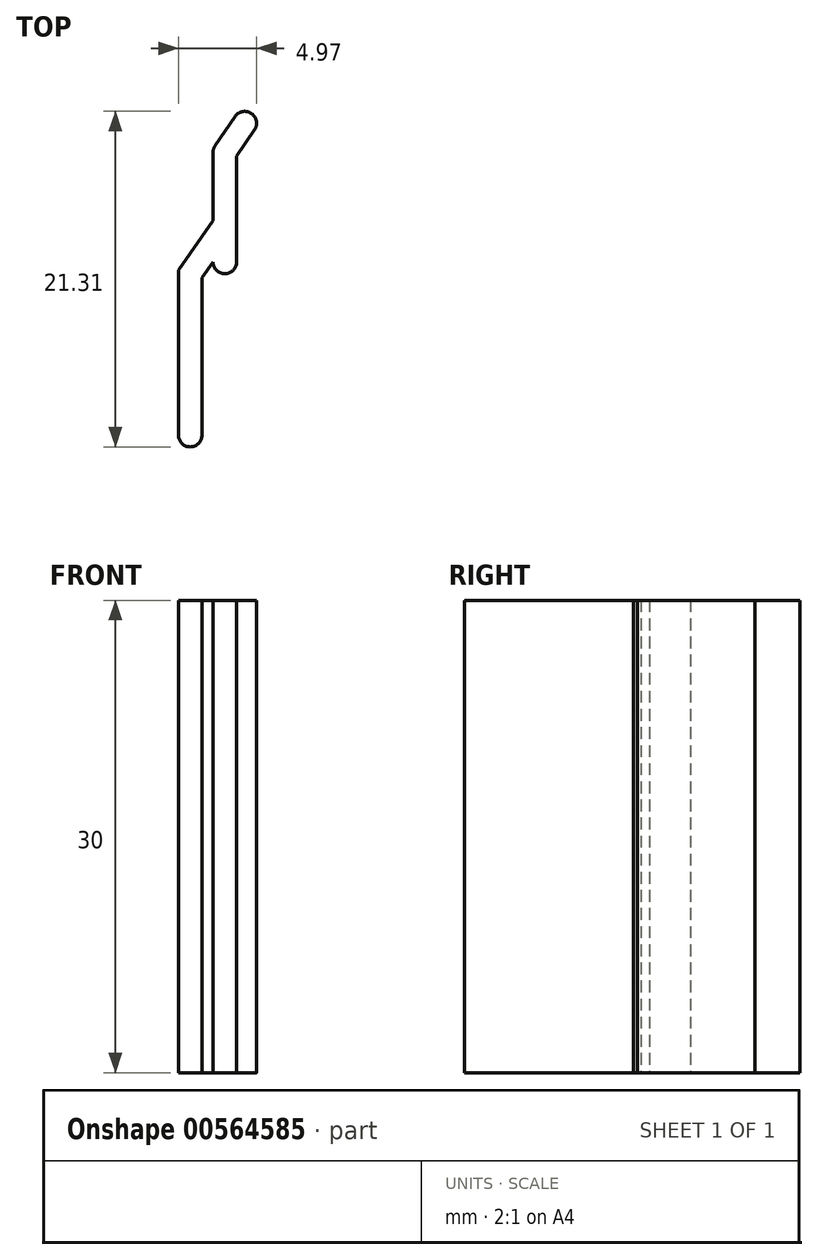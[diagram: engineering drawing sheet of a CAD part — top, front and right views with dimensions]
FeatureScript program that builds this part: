
annotation { "Feature Type Name" : "Feature", "Feature Type Description" : "" }
export const myFeature = defineFeature(function(context is Context, id is Id, definition is map)
    precondition{}
    {
        {
            var Q0;
            Q0=qCreatedBy(makeId("Top.planeOp"),FACE);
            var sketch = newSketch(context, id + "F0", { "sketchPlane" : qUnion([Q0])});
            skLineSegment(sketch, "E0", {"start": v(0, 0) * mm, "end": v(0, -6.95) * mm, "construction": true});
            skLineSegment(sketch, "E1", {"start": v(0, 0) * mm, "end": v(1.27, 1.86) * mm, "construction": true});
            skArc(sketch, "E2.0.startCap", {"start": v(-0.75, 0) * mm, "mid": v(-0.72, 0.22) * mm, "end": v(-0.62, 0.42) * mm});
            skArc(sketch, "E2.0.endCap", {"start": v(0.75, -6.95) * mm, "mid": v(0, -7.7) * mm, "end": v(-0.75, -6.95) * mm});
            skLineSegment(sketch, "E2.0.left", {"start": v(0.75, -0.23) * mm, "end": v(0.75, -6.95) * mm});
            skLineSegment(sketch, "E2.0.right", {"start": v(-0.75, 0) * mm, "end": v(-0.75, -6.95) * mm});
            skArc(sketch, "E2.1.endCap", {"start": v(0.65, 2.28) * mm, "mid": v(1.69, 2.48) * mm, "end": v(1.89, 1.44) * mm});
            skLineSegment(sketch, "E2.1.left", {"start": v(-0.62, 0.42) * mm, "end": v(0.65, 2.28) * mm});
            skLineSegment(sketch, "E2.1.right", {"start": v(0.75, -0.23) * mm, "end": v(1.89, 1.44) * mm});
            skSolve(sketch);
        }
        {
            var Q0;
            Q0=qCreatedBy(makeId("Top.planeOp"),FACE);
            var sketch = newSketch(context, id + "F1", { "sketchPlane" : qUnion([Q0])});
            skLineSegment(sketch, "E3", {"start": v(-1.45, -7.95) * mm, "end": v(-1.45, -17.95) * mm});
            skPoint(sketch, "E4.0", {"position": v(-0.75, -6.95) * mm});
            skLineSegment(sketch, "E5.0", {"start": v(-0.75, 0) * mm, "end": v(-0.75, -6.95) * mm, "construction": true});
            skLineSegment(sketch, "E6", {"start": v(-0.75, -4.33) * mm, "end": v(-0.75, -6.95) * mm});
            skLineSegment(sketch, "E7", {"start": v(-0.75, -4.33) * mm, "end": v(-2.95, -7.48) * mm});
            skLineSegment(sketch, "E8", {"start": v(-2.95, -7.48) * mm, "end": v(-2.95, -17.95) * mm});
            skArc(sketch, "E9", {"start": v(-2.95, -17.95) * mm, "mid": v(-2.2, -18.7) * mm, "end": v(-1.45, -17.95) * mm});
            skLineSegment(sketch, "E10", {"start": v(-1.45, -7.95) * mm, "end": v(-0.75, -6.95) * mm});
            skLineSegment(sketch, "E11", {"start": v(-0.75, -6.95) * mm, "end": v(0.75, -6.95) * mm, "construction": true});
            skPoint(sketch, "E12", {"position": v(-0.75, -3.48) * mm});
            skLineSegment(sketch, "E13", {"start": v(-2.68, -7.09) * mm, "end": v(-1.45, -7.95) * mm, "construction": true});
            skSolve(sketch);
        }
        {
            var Q0;
            Q0 = qSketchRegion(id + "F0", true);
            extrude(context, id + "F2", {"entities" : qUnion([Q0]), "depth" : 30 * mm, "offsetDistance" : 25 * mm});
        }
        {
            var Q0;
            Q0 = qSketchRegion(id + "F1", true);
            var Q1;
            Q1=makeQuery(id+"F2.opExtrude","CAP_FACE",FACE,{"disambiguationData":[OSD([sQuery(id+"F0.wireOp",EDGE,"E2.0.endCap"),sQuery(id+"F0.wireOp",EDGE,"E2.0.left"),sQuery(id+"F0.wireOp",EDGE,"E2.0.right"),sQuery(id+"F0.wireOp",EDGE,"E2.1.endCap"),sQuery(id+"F0.wireOp",EDGE,"E2.1.left"),sQuery(id+"F0.wireOp",EDGE,"E2.1.right"),sQuery(id+"F0.wireOp",EDGE,"E2.0.startCap")])],"isStart":false});
            extrude(context, id + "F3", {"entities" : qUnion([Q0]), "operationType" : NewBodyOperationType.ADD, "endBound" : BoundingType.UP_TO_SURFACE, "depth" : 25 * mm, "endBoundEntityFace" : qUnion([Q1]), "offsetDistance" : 25 * mm});
        }
    });
